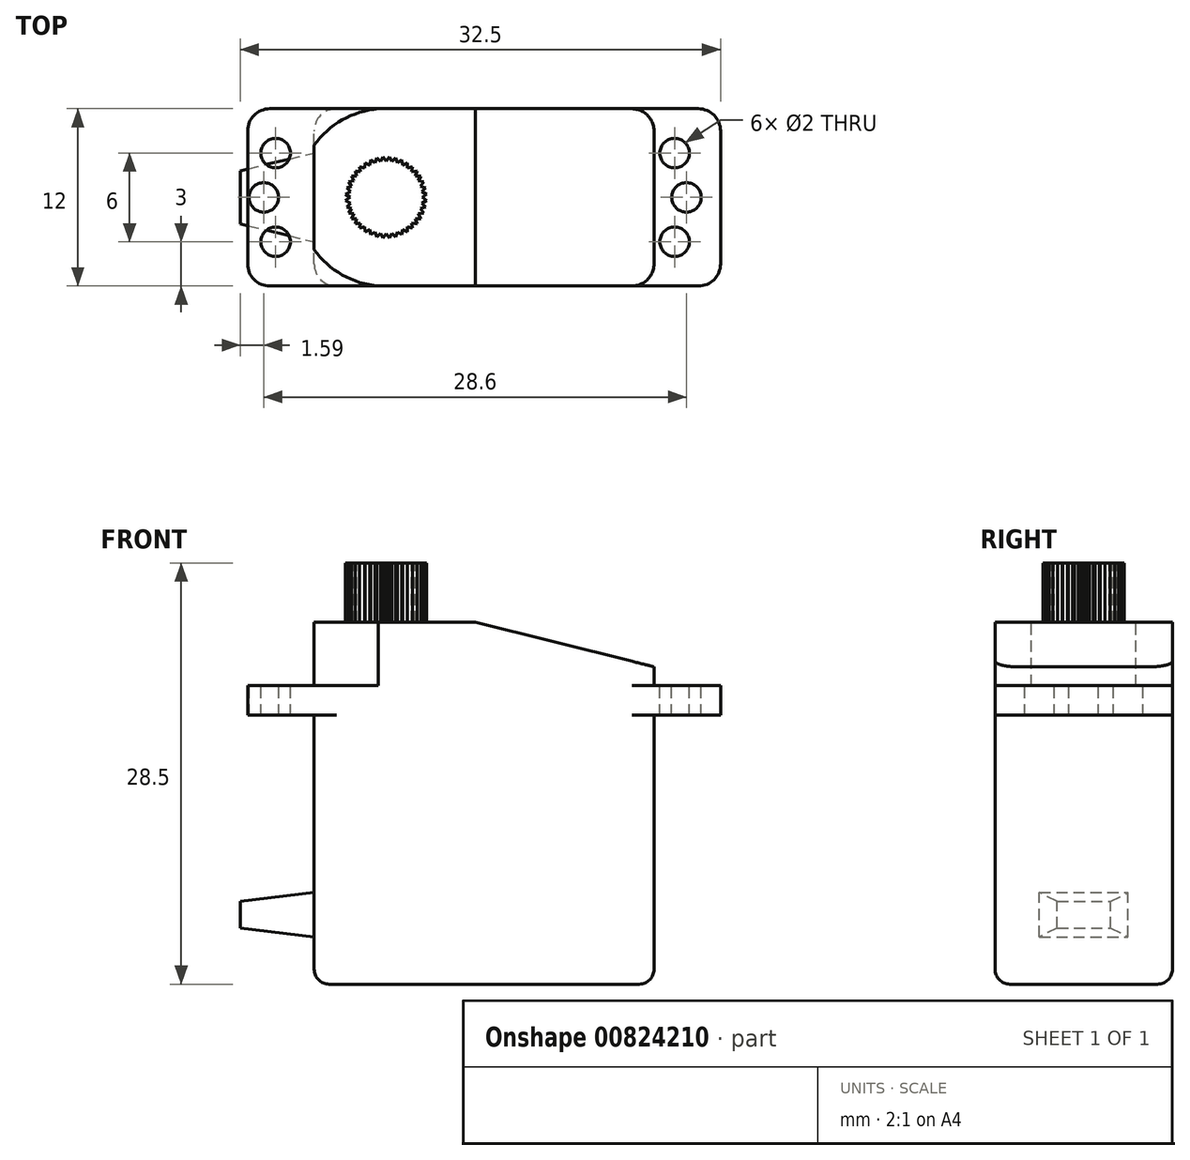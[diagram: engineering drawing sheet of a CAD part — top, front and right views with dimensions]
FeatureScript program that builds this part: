
annotation { "Feature Type Name" : "Feature", "Feature Type Description" : "" }
export const myFeature = defineFeature(function(context is Context, id is Id, definition is map)
    precondition{}
    {
        {
            var Q0;
            Q0=qCreatedBy(makeId("Front.planeOp"),FACE);
            var sketch = newSketch(context, id + "F0", { "sketchPlane" : qUnion([Q0])});
            skLineSegment(sketch, "E0", {"start": v(-16, 15.1) * mm, "end": v(17, -14.2) * mm, "construction": true});
            skSolve(sketch);
        }
        {
            var Q0;
            Q0=qCreatedBy(makeId("Front.planeOp"),FACE);
            var sketch = newSketch(context, id + "F1", { "sketchPlane" : qUnion([Q0])});
            skLineSegment(sketch, "E1", {"start": v(-10.9, -14.1) * mm, "end": v(-10.9, 4.1) * mm});
            skLineSegment(sketch, "E2", {"start": v(-10.9, 4.1) * mm, "end": v(-15.4, 4.1) * mm});
            skLineSegment(sketch, "E3", {"start": v(-15.4, 4.1) * mm, "end": v(-15.4, 6.1) * mm});
            skLineSegment(sketch, "E4", {"start": v(-15.4, 6.1) * mm, "end": v(-10.9, 6.1) * mm});
            skLineSegment(sketch, "E5", {"start": v(-10.9, 6.1) * mm, "end": v(-10.9, 10.4) * mm});
            skLineSegment(sketch, "E6", {"start": v(-10.9, 10.4) * mm, "end": v(0, 10.4) * mm});
            skLineSegment(sketch, "E7", {"start": v(0, 10.4) * mm, "end": v(12.1, 7.38) * mm});
            skLineSegment(sketch, "E8", {"start": v(12.1, 7.38) * mm, "end": v(12.1, 6.1) * mm});
            skLineSegment(sketch, "E9", {"start": v(12.1, 6.1) * mm, "end": v(16.6, 6.1) * mm});
            skLineSegment(sketch, "E10", {"start": v(16.6, 6.1) * mm, "end": v(16.6, 4.1) * mm});
            skLineSegment(sketch, "E11", {"start": v(16.6, 4.1) * mm, "end": v(12.1, 4.1) * mm});
            skLineSegment(sketch, "E12", {"start": v(12.1, 4.1) * mm, "end": v(12.1, -14.1) * mm});
            skLineSegment(sketch, "E13", {"start": v(12.1, -14.1) * mm, "end": v(-10.9, -14.1) * mm});
            skSolve(sketch);
        }
        {
            var Q0;
            Q0=makeQuery(id+"F1.imprint","IMPRINT",FACE,{"disambiguationData":[TD([[makeQuery(id+"F1.imprint","IMPRINT",EDGE,{"derivedFrom":sQuery(id+"F1.wireOp",EDGE,"E1")}),-1.0]])]});
            extrude(context, id + "F2", {"entities" : qUnion([Q0]), "depth" : 12 * mm, "offsetDistance" : 25 * mm, "symmetric" : true});
        }
        {
            var Q0;
            Q0=makeQuery(id+"F2.opExtrude","SWEPT_FACE",FACE,{"disambiguationData":[OSD([sQuery(id+"F1.wireOp",EDGE,"E4")])]});
            cPlane(context, id + "F3", {"entities" : qUnion([Q0]), "cplaneType" : CPlaneType.OFFSET, "offset" : 0 * mm, "width" : 150 * mm, "height" : 150 * mm});
        }
        {
            var Q0;
            Q0=qCreatedBy(id+"F3.planeOp",FACE);
            var sketch = newSketch(context, id + "F4", { "sketchPlane" : qUnion([Q0])});
            skLineSegment(sketch, "E14", {"start": v(-13.5, 5.08) * mm, "end": v(-13.5, -5.4) * mm, "construction": true});
            skLineSegment(sketch, "E15", {"start": v(13.5, 5.08) * mm, "end": v(13.5, -5.19) * mm, "construction": true});
            skLineSegment(sketch, "E16", {"start": v(0, 4.66) * mm, "end": v(0, -5.13) * mm, "construction": true});
            skCircle(sketch, "E17", {"center": v(-13.5, 3) * mm, "radius": 1 * mm});
            skCircle(sketch, "E18", {"center": v(-13.5, -3) * mm, "radius": 1 * mm});
            skLineSegment(sketch, "E19", {"start": v(0, 0) * mm, "end": v(-7.33, 0) * mm, "construction": true});
            skCircle(sketch, "E20.MirrorC", {"center": v(13.5, 3) * mm, "radius": 1 * mm});
            skCircle(sketch, "E21.MirrorC", {"center": v(13.5, -3) * mm, "radius": 1 * mm});
            skCircle(sketch, "E22", {"center": v(-14.3, 0) * mm, "radius": 1 * mm});
            skCircle(sketch, "E23", {"center": v(14.3, 0) * mm, "radius": 1 * mm});
            skSolve(sketch);
        }
        {
            var Q0;
            Q0 = qSketchRegion(id + "F4", true);
            extrude(context, id + "F5", {"entities" : qUnion([Q0]), "operationType" : NewBodyOperationType.REMOVE, "endBound" : BoundingType.UP_TO_NEXT, "oppositeDirection" : true, "depth" : 25 * mm, "offsetDistance" : 25 * mm});
        }
        {
            var Q0;
            Q0=makeQuery(id+"F2.opExtrude","SWEPT_FACE",FACE,{"disambiguationData":[OSD([sQuery(id+"F1.wireOp",EDGE,"E6")])]});
            var sketch = newSketch(context, id + "F6", { "sketchPlane" : qUnion([Q0])});
            skCircle(sketch, "E24", {"center": v(-6.02, 0) * mm, "radius": 6.02 * mm});
            skSolve(sketch);
        }
        {
            var Q0;
            {var subQ0=sQuery(id+"F6.wireOp",EDGE,"E24");var subQ1=sQuery(id+"F1.wireOp",EDGE,"E6");var subQ2=makeQuery(id+"F2.opExtrude","CAP_EDGE",EDGE,{"disambiguationData":[OSD([subQ1])],"isStart":true});var subQ3=makeQuery(id+"F6.imprint","INTERSECT",VERTEX,{"disambiguationData":[OD(1.0)],"derivedFrom":[subQ2,subQ0]});Q0=makeQuery(id+"F6.imprint","IMPRINT",FACE,{"disambiguationData":[TD([[makeQuery(id+"F6.imprint","IMPRINT",EDGE,{"disambiguationData":[TD([[subQ3,-1.0]])],"derivedFrom":subQ0}),-1.0]])]});}
            var Q1;
            {var subQ0=sQuery(id+"F6.wireOp",EDGE,"E24");var subQ1=sQuery(id+"F1.wireOp",EDGE,"E6");var subQ4=makeQuery(id+"F2.opExtrude","CAP_EDGE",EDGE,{"disambiguationData":[OSD([subQ1])],"isStart":false});var subQ5=makeQuery(id+"F6.imprint","INTERSECT",VERTEX,{"disambiguationData":[OD(0.0)],"derivedFrom":[subQ4,subQ0]});Q1=makeQuery(id+"F6.imprint","IMPRINT",FACE,{"disambiguationData":[TD([[makeQuery(id+"F6.imprint","IMPRINT",EDGE,{"disambiguationData":[TD([[subQ5,1.0]])],"derivedFrom":subQ0}),-1.0]])]});}
            var Q2;
            Q2=makeQuery(id+"F2.opExtrude","SWEPT_FACE",FACE,{"disambiguationData":[OSD([sQuery(id+"F1.wireOp",EDGE,"E4")])]});
            extrude(context, id + "F7", {"entities" : qUnion([Q0, Q1]), "operationType" : NewBodyOperationType.REMOVE, "endBound" : BoundingType.UP_TO_SURFACE, "oppositeDirection" : true, "depth" : 25 * mm, "endBoundEntityFace" : qUnion([Q2]), "offsetDistance" : 25 * mm});
        }
        {
            var Q0;
            {var subQ0=sQuery(id+"F6.wireOp",EDGE,"E24");var subQ1=sQuery(id+"F1.wireOp",EDGE,"E6");var subQ8=makeQuery(id+"F2.opExtrude","CAP_EDGE",EDGE,{"disambiguationData":[OSD([subQ1])],"isStart":true});var subQ11=makeQuery(id+"F6.imprint","INTERSECT",VERTEX,{"disambiguationData":[OD(0.0)],"derivedFrom":[subQ8,subQ0]});Q0=makeQuery(id+"F6.imprint","IMPRINT",FACE,{"disambiguationData":[TD([[makeQuery(id+"F6.imprint","IMPRINT",EDGE,{"disambiguationData":[TD([[subQ11,1.0]])],"derivedFrom":subQ8}),-1.0]])]});}
            var sketch = newSketch(context, id + "F8", { "sketchPlane" : qUnion([Q0])});
            skCircle(sketch, "E25", {"center": v(-6.02, 0) * mm, "radius": 2.75 * mm});
            skSolve(sketch);
        }
        {
            var Q0;
            Q0=makeQuery(id+"F8.imprint","IMPRINT",FACE,{"disambiguationData":[TD([[makeQuery(id+"F8.imprint","IMPRINT",EDGE,{"derivedFrom":sQuery(id+"F8.wireOp",EDGE,"E25")}),1.0]])]});
            extrude(context, id + "F9", {"entities" : qUnion([Q0]), "depth" : 4 * mm, "offsetDistance" : 25 * mm});
        }
        {
            var Q0;
            Q0=makeQuery(id+"F9.opExtrude","CAP_FACE",FACE,{"disambiguationData":[OSD([sQuery(id+"F8.wireOp",EDGE,"E25")])],"isStart":false});
            var sketch = newSketch(context, id + "F10", { "sketchPlane" : qUnion([Q0])});
            skCircle(sketch, "E26.0", {"center": v(-6.02, 0) * mm, "radius": 2.45 * mm, "construction": true});
            skCircle(sketch, "E27.0", {"center": v(-6.02, 0) * mm, "radius": 7.75 * mm});
            skLineSegment(sketch, "E28", {"start": v(-6.02, 0) * mm, "end": v(-6.02, 2.75) * mm, "construction": true});
            skLineSegment(sketch, "E29", {"start": v(-6.02, 0) * mm, "end": v(-5.8, 2.74) * mm, "construction": true});
            skLineSegment(sketch, "E30", {"start": v(-6.02, 0) * mm, "end": v(-6.24, 2.74) * mm, "construction": true});
            skLineSegment(sketch, "E31", {"start": v(-6.24, 2.74) * mm, "end": v(-6.02, 2.45) * mm});
            skLineSegment(sketch, "E32", {"start": v(-6.02, 2.45) * mm, "end": v(-5.8, 2.74) * mm});
            skLineSegment(sketch, "E33.1.0", {"start": v(-6.67, 2.67) * mm, "end": v(-6.4, 2.42) * mm});
            skLineSegment(sketch, "E33.1.1", {"start": v(-6.4, 2.42) * mm, "end": v(-6.24, 2.74) * mm});
            skLineSegment(sketch, "E33.2.0", {"start": v(-7.08, 2.54) * mm, "end": v(-6.78, 2.33) * mm});
            skLineSegment(sketch, "E33.2.1", {"start": v(-6.78, 2.33) * mm, "end": v(-6.67, 2.67) * mm});
            skLineSegment(sketch, "E33.3.0", {"start": v(-7.46, 2.34) * mm, "end": v(-7.14, 2.18) * mm});
            skLineSegment(sketch, "E33.3.1", {"start": v(-7.14, 2.18) * mm, "end": v(-7.08, 2.54) * mm});
            skLineSegment(sketch, "E33.4.0", {"start": v(-7.8, 2.1) * mm, "end": v(-7.46, 1.98) * mm});
            skLineSegment(sketch, "E33.4.1", {"start": v(-7.46, 1.98) * mm, "end": v(-7.46, 2.34) * mm});
            skLineSegment(sketch, "E33.5.0", {"start": v(-8.11, 1.79) * mm, "end": v(-7.76, 1.73) * mm});
            skLineSegment(sketch, "E33.5.1", {"start": v(-7.76, 1.73) * mm, "end": v(-7.8, 2.1) * mm});
            skLineSegment(sketch, "E33.6.0", {"start": v(-8.37, 1.44) * mm, "end": v(-8, 1.44) * mm});
            skLineSegment(sketch, "E33.6.1", {"start": v(-8, 1.44) * mm, "end": v(-8.11, 1.79) * mm});
            skLineSegment(sketch, "E33.7.0", {"start": v(-8.56, 1.05) * mm, "end": v(-8.2, 1.11) * mm});
            skLineSegment(sketch, "E33.7.1", {"start": v(-8.2, 1.11) * mm, "end": v(-8.37, 1.44) * mm});
            skLineSegment(sketch, "E33.8.0", {"start": v(-8.7, 0.64) * mm, "end": v(-8.35, 0.76) * mm});
            skLineSegment(sketch, "E33.8.1", {"start": v(-8.35, 0.76) * mm, "end": v(-8.56, 1.05) * mm});
            skLineSegment(sketch, "E33.9.0", {"start": v(-8.76, 0.22) * mm, "end": v(-8.44, 0.38) * mm});
            skLineSegment(sketch, "E33.9.1", {"start": v(-8.44, 0.38) * mm, "end": v(-8.7, 0.64) * mm});
            skLineSegment(sketch, "E33.10.0", {"start": v(-8.76, -0.22) * mm, "end": v(-8.47, 0) * mm});
            skLineSegment(sketch, "E33.10.1", {"start": v(-8.47, 0) * mm, "end": v(-8.76, 0.22) * mm});
            skLineSegment(sketch, "E33.11.0", {"start": v(-8.7, -0.64) * mm, "end": v(-8.44, -0.38) * mm});
            skLineSegment(sketch, "E33.11.1", {"start": v(-8.44, -0.38) * mm, "end": v(-8.76, -0.22) * mm});
            skLineSegment(sketch, "E33.12.0", {"start": v(-8.56, -1.05) * mm, "end": v(-8.35, -0.76) * mm});
            skLineSegment(sketch, "E33.12.1", {"start": v(-8.35, -0.76) * mm, "end": v(-8.7, -0.64) * mm});
            skLineSegment(sketch, "E33.13.0", {"start": v(-8.37, -1.44) * mm, "end": v(-8.2, -1.11) * mm});
            skLineSegment(sketch, "E33.13.1", {"start": v(-8.2, -1.11) * mm, "end": v(-8.56, -1.05) * mm});
            skLineSegment(sketch, "E33.14.0", {"start": v(-8.11, -1.79) * mm, "end": v(-8, -1.44) * mm});
            skLineSegment(sketch, "E33.14.1", {"start": v(-8, -1.44) * mm, "end": v(-8.37, -1.44) * mm});
            skLineSegment(sketch, "E33.15.0", {"start": v(-7.8, -2.1) * mm, "end": v(-7.76, -1.73) * mm});
            skLineSegment(sketch, "E33.15.1", {"start": v(-7.76, -1.73) * mm, "end": v(-8.11, -1.79) * mm});
            skLineSegment(sketch, "E33.16.0", {"start": v(-7.46, -2.34) * mm, "end": v(-7.46, -1.98) * mm});
            skLineSegment(sketch, "E33.16.1", {"start": v(-7.46, -1.98) * mm, "end": v(-7.8, -2.1) * mm});
            skLineSegment(sketch, "E33.17.0", {"start": v(-7.08, -2.54) * mm, "end": v(-7.14, -2.18) * mm});
            skLineSegment(sketch, "E33.17.1", {"start": v(-7.14, -2.18) * mm, "end": v(-7.46, -2.34) * mm});
            skLineSegment(sketch, "E33.18.0", {"start": v(-6.67, -2.67) * mm, "end": v(-6.78, -2.33) * mm});
            skLineSegment(sketch, "E33.18.1", {"start": v(-6.78, -2.33) * mm, "end": v(-7.08, -2.54) * mm});
            skLineSegment(sketch, "E33.19.0", {"start": v(-6.24, -2.74) * mm, "end": v(-6.4, -2.42) * mm});
            skLineSegment(sketch, "E33.19.1", {"start": v(-6.4, -2.42) * mm, "end": v(-6.67, -2.67) * mm});
            skLineSegment(sketch, "E33.20.0", {"start": v(-5.8, -2.74) * mm, "end": v(-6.02, -2.45) * mm});
            skLineSegment(sketch, "E33.20.1", {"start": v(-6.02, -2.45) * mm, "end": v(-6.24, -2.74) * mm});
            skLineSegment(sketch, "E33.21.0", {"start": v(-5.38, -2.67) * mm, "end": v(-5.64, -2.42) * mm});
            skLineSegment(sketch, "E33.21.1", {"start": v(-5.64, -2.42) * mm, "end": v(-5.8, -2.74) * mm});
            skLineSegment(sketch, "E33.22.0", {"start": v(-4.97, -2.54) * mm, "end": v(-5.27, -2.33) * mm});
            skLineSegment(sketch, "E33.22.1", {"start": v(-5.27, -2.33) * mm, "end": v(-5.38, -2.67) * mm});
            skLineSegment(sketch, "E33.23.0", {"start": v(-4.59, -2.34) * mm, "end": v(-4.91, -2.18) * mm});
            skLineSegment(sketch, "E33.23.1", {"start": v(-4.91, -2.18) * mm, "end": v(-4.97, -2.54) * mm});
            skLineSegment(sketch, "E33.24.0", {"start": v(-4.24, -2.1) * mm, "end": v(-4.58, -1.98) * mm});
            skLineSegment(sketch, "E33.24.1", {"start": v(-4.58, -1.98) * mm, "end": v(-4.59, -2.34) * mm});
            skLineSegment(sketch, "E33.25.0", {"start": v(-3.93, -1.79) * mm, "end": v(-4.3, -1.73) * mm});
            skLineSegment(sketch, "E33.25.1", {"start": v(-4.3, -1.73) * mm, "end": v(-4.24, -2.1) * mm});
            skLineSegment(sketch, "E33.26.0", {"start": v(-3.68, -1.44) * mm, "end": v(-4.04, -1.44) * mm});
            skLineSegment(sketch, "E33.26.1", {"start": v(-4.04, -1.44) * mm, "end": v(-3.93, -1.79) * mm});
            skLineSegment(sketch, "E33.27.0", {"start": v(-3.48, -1.05) * mm, "end": v(-3.84, -1.11) * mm});
            skLineSegment(sketch, "E33.27.1", {"start": v(-3.84, -1.11) * mm, "end": v(-3.68, -1.44) * mm});
            skLineSegment(sketch, "E33.28.0", {"start": v(-3.35, -0.64) * mm, "end": v(-3.7, -0.76) * mm});
            skLineSegment(sketch, "E33.28.1", {"start": v(-3.7, -0.76) * mm, "end": v(-3.48, -1.05) * mm});
            skLineSegment(sketch, "E33.29.0", {"start": v(-3.28, -0.22) * mm, "end": v(-3.6, -0.38) * mm});
            skLineSegment(sketch, "E33.29.1", {"start": v(-3.6, -0.38) * mm, "end": v(-3.35, -0.64) * mm});
            skLineSegment(sketch, "E33.30.0", {"start": v(-3.28, 0.22) * mm, "end": v(-3.57, 0) * mm});
            skLineSegment(sketch, "E33.30.1", {"start": v(-3.57, 0) * mm, "end": v(-3.28, -0.22) * mm});
            skLineSegment(sketch, "E33.31.0", {"start": v(-3.35, 0.64) * mm, "end": v(-3.6, 0.38) * mm});
            skLineSegment(sketch, "E33.31.1", {"start": v(-3.6, 0.38) * mm, "end": v(-3.28, 0.22) * mm});
            skLineSegment(sketch, "E33.32.0", {"start": v(-3.48, 1.05) * mm, "end": v(-3.7, 0.76) * mm});
            skLineSegment(sketch, "E33.32.1", {"start": v(-3.7, 0.76) * mm, "end": v(-3.35, 0.64) * mm});
            skLineSegment(sketch, "E33.33.0", {"start": v(-3.68, 1.44) * mm, "end": v(-3.84, 1.11) * mm});
            skLineSegment(sketch, "E33.33.1", {"start": v(-3.84, 1.11) * mm, "end": v(-3.48, 1.05) * mm});
            skLineSegment(sketch, "E33.34.0", {"start": v(-3.93, 1.79) * mm, "end": v(-4.04, 1.44) * mm});
            skLineSegment(sketch, "E33.34.1", {"start": v(-4.04, 1.44) * mm, "end": v(-3.68, 1.44) * mm});
            skLineSegment(sketch, "E33.35.0", {"start": v(-4.24, 2.1) * mm, "end": v(-4.3, 1.73) * mm});
            skLineSegment(sketch, "E33.35.1", {"start": v(-4.3, 1.73) * mm, "end": v(-3.93, 1.79) * mm});
            skLineSegment(sketch, "E33.36.0", {"start": v(-4.59, 2.34) * mm, "end": v(-4.58, 1.98) * mm});
            skLineSegment(sketch, "E33.36.1", {"start": v(-4.58, 1.98) * mm, "end": v(-4.24, 2.1) * mm});
            skLineSegment(sketch, "E33.37.0", {"start": v(-4.97, 2.54) * mm, "end": v(-4.91, 2.18) * mm});
            skLineSegment(sketch, "E33.37.1", {"start": v(-4.91, 2.18) * mm, "end": v(-4.59, 2.34) * mm});
            skLineSegment(sketch, "E33.38.0", {"start": v(-5.38, 2.67) * mm, "end": v(-5.27, 2.33) * mm});
            skLineSegment(sketch, "E33.38.1", {"start": v(-5.27, 2.33) * mm, "end": v(-4.97, 2.54) * mm});
            skLineSegment(sketch, "E33.39.0", {"start": v(-5.8, 2.74) * mm, "end": v(-5.64, 2.42) * mm});
            skLineSegment(sketch, "E33.39.1", {"start": v(-5.64, 2.42) * mm, "end": v(-5.38, 2.67) * mm});
            skSolve(sketch);
        }
        {
            var Q0;
            Q0 = qSketchRegion(id + "F10", true);
            var Q1;
            Q1=makeQuery(id+"F2.opExtrude","SWEPT_FACE",FACE,{"disambiguationData":[OSD([sQuery(id+"F1.wireOp",EDGE,"E6")])]});
            extrude(context, id + "F11", {"entities" : qUnion([Q0]), "operationType" : NewBodyOperationType.REMOVE, "endBound" : BoundingType.UP_TO_SURFACE, "oppositeDirection" : true, "depth" : 25 * mm, "endBoundEntityFace" : qUnion([Q1]), "offsetDistance" : 25 * mm});
        }
        {
            var Q0;
            Q0=makeQuery(id+"F2.opExtrude","SWEPT_FACE",FACE,{"disambiguationData":[OSD([sQuery(id+"F1.wireOp",EDGE,"E1")])]});
            var sketch = newSketch(context, id + "F12", { "sketchPlane" : qUnion([Q0])});
            skLineSegment(sketch, "E34.bottom", {"start": v(3, -10.9) * mm, "end": v(-3, -10.9) * mm});
            skLineSegment(sketch, "E34.top", {"start": v(3, -7.9) * mm, "end": v(-3, -7.9) * mm});
            skLineSegment(sketch, "E34.left", {"start": v(3, -10.9) * mm, "end": v(3, -7.9) * mm});
            skLineSegment(sketch, "E34.right", {"start": v(-3, -10.9) * mm, "end": v(-3, -7.9) * mm});
            skPoint(sketch, "E34.middle", {"position": v(0, -9.4) * mm});
            skSolve(sketch);
        }
        {
            var Q0;
            Q0=makeQuery(id+"F12.imprint","IMPRINT",FACE,{"disambiguationData":[TD([[makeQuery(id+"F12.imprint","IMPRINT",EDGE,{"derivedFrom":sQuery(id+"F12.wireOp",EDGE,"E34.bottom")}),1.0]])]});
            cPlane(context, id + "F13", {"entities" : qUnion([Q0]), "cplaneType" : CPlaneType.OFFSET, "offset" : 5 * mm, "width" : 150 * mm, "height" : 150 * mm});
        }
        {
            var Q0;
            Q0=qCreatedBy(id+"F13.planeOp",FACE);
            var sketch = newSketch(context, id + "F14", { "sketchPlane" : qUnion([Q0])});
            skLineSegment(sketch, "E35.bottom", {"start": v(1.8, -10.3) * mm, "end": v(-1.8, -10.3) * mm});
            skLineSegment(sketch, "E35.top", {"start": v(1.8, -8.5) * mm, "end": v(-1.8, -8.5) * mm});
            skLineSegment(sketch, "E35.left", {"start": v(1.8, -10.3) * mm, "end": v(1.8, -8.5) * mm});
            skLineSegment(sketch, "E35.right", {"start": v(-1.8, -10.3) * mm, "end": v(-1.8, -8.5) * mm});
            skPoint(sketch, "E35.middle", {"position": v(0, -9.4) * mm});
            skSolve(sketch);
        }
        {
            var Q1;
            Q1=makeQuery(id+"F14.imprint","IMPRINT",FACE,{"disambiguationData":[TD([[makeQuery(id+"F14.imprint","IMPRINT",EDGE,{"derivedFrom":sQuery(id+"F14.wireOp",EDGE,"E35.bottom")}),-1.0]])]});
            var Q2;
            Q2=makeQuery(id+"F12.imprint","IMPRINT",FACE,{"disambiguationData":[TD([[makeQuery(id+"F12.imprint","IMPRINT",EDGE,{"derivedFrom":sQuery(id+"F12.wireOp",EDGE,"E34.bottom")}),-1.0]])]});
            loft(context, id + "F15", {"operationType" : NewBodyOperationType.ADD, "sheetProfilesArray" : [{ "sheetProfileEntities" : qUnion([Q1]) }, { "sheetProfileEntities" : qUnion([Q2]) }]});
        }
        {
            var Q0;
            Q0=makeQuery(id+"F2.opExtrude","CAP_EDGE",EDGE,{"disambiguationData":[OSD([sQuery(id+"F1.wireOp",EDGE,"E3")])],"isStart":false});
            var Q1;
            Q1=makeQuery(id+"F2.opExtrude","CAP_EDGE",EDGE,{"disambiguationData":[OSD([sQuery(id+"F1.wireOp",EDGE,"E3")])],"isStart":true});
            var Q2;
            {var subQ0=sQuery(id+"F6.wireOp",EDGE,"E24");var subQ1=sQuery(id+"F1.wireOp",EDGE,"E6");var subQ2=sQuery(id+"F1.wireOp",EDGE,"E5");Q2=makeQuery(id+"F7.boolean.opBoolean","COPY",EDGE,{"derivedFrom":makeQuery(id+"F7.opExtrude","SWEPT_EDGE",EDGE,{"disambiguationData":[OSD([subQ2,subQ1,subQ0]),TDD([makeQuery(id+"F6.imprint","INTERSECT",VERTEX,{"disambiguationData":[OD(1.0)],"derivedFrom":[makeQuery(id+"F2.opExtrude","SWEPT_EDGE",EDGE,{"disambiguationData":[OSD([subQ2,subQ1])]}),subQ0]})])]})});}
            var Q3;
            {var subQ0=sQuery(id+"F6.wireOp",EDGE,"E24");var subQ1=sQuery(id+"F1.wireOp",EDGE,"E6");var subQ2=sQuery(id+"F1.wireOp",EDGE,"E5");Q3=makeQuery(id+"F7.boolean.opBoolean","COPY",EDGE,{"derivedFrom":makeQuery(id+"F7.opExtrude","SWEPT_EDGE",EDGE,{"disambiguationData":[OSD([subQ2,subQ1,subQ0]),TDD([makeQuery(id+"F6.imprint","INTERSECT",VERTEX,{"disambiguationData":[OD(0.0)],"derivedFrom":[makeQuery(id+"F2.opExtrude","SWEPT_EDGE",EDGE,{"disambiguationData":[OSD([subQ2,subQ1])]}),subQ0]})])]})});}
            var Q4;
            Q4=makeQuery(id+"F2.opExtrude","CAP_EDGE",EDGE,{"disambiguationData":[OSD([sQuery(id+"F1.wireOp",EDGE,"E10")])],"isStart":false});
            var Q5;
            Q5=makeQuery(id+"F2.opExtrude","CAP_EDGE",EDGE,{"disambiguationData":[OSD([sQuery(id+"F1.wireOp",EDGE,"E10")])],"isStart":true});
            var Q6;
            Q6=makeQuery(id+"F2.opExtrude","CAP_EDGE",EDGE,{"disambiguationData":[OSD([sQuery(id+"F1.wireOp",EDGE,"E12")])],"isStart":false});
            var Q7;
            Q7=makeQuery(id+"F2.opExtrude","CAP_EDGE",EDGE,{"disambiguationData":[OSD([sQuery(id+"F1.wireOp",EDGE,"E8")])],"isStart":false});
            var Q8;
            Q8=makeQuery(id+"F2.opExtrude","CAP_EDGE",EDGE,{"disambiguationData":[OSD([sQuery(id+"F1.wireOp",EDGE,"E8")])],"isStart":true});
            var Q9;
            Q9=makeQuery(id+"F2.opExtrude","CAP_EDGE",EDGE,{"disambiguationData":[OSD([sQuery(id+"F1.wireOp",EDGE,"E12")])],"isStart":true});
            var Q10;
            Q10=makeQuery(id+"F2.opExtrude","CAP_EDGE",EDGE,{"disambiguationData":[OSD([sQuery(id+"F1.wireOp",EDGE,"E1")])],"isStart":true});
            var Q11;
            Q11=makeQuery(id+"F2.opExtrude","CAP_EDGE",EDGE,{"disambiguationData":[OSD([sQuery(id+"F1.wireOp",EDGE,"E1")])],"isStart":false});
            fillet(context, id + "F16", {"entities" : qUnion([Q0, Q1, Q2, Q3, Q4, Q5, Q6, Q7, Q8, Q9, Q10, Q11]), "radius" : 1.5 * mm, "tangentPropagation" : true, "allowEdgeOverflow" : false});
        }
        {
            var Q0;
            Q0=makeQuery(id+"F2.opExtrude","SWEPT_FACE",FACE,{"disambiguationData":[OSD([sQuery(id+"F1.wireOp",EDGE,"E13")])]});
            fillet(context, id + "F17", {"entities" : qUnion([Q0]), "radius" : 1 * mm, "tangentPropagation" : true, "allowEdgeOverflow" : false});
        }
    });
